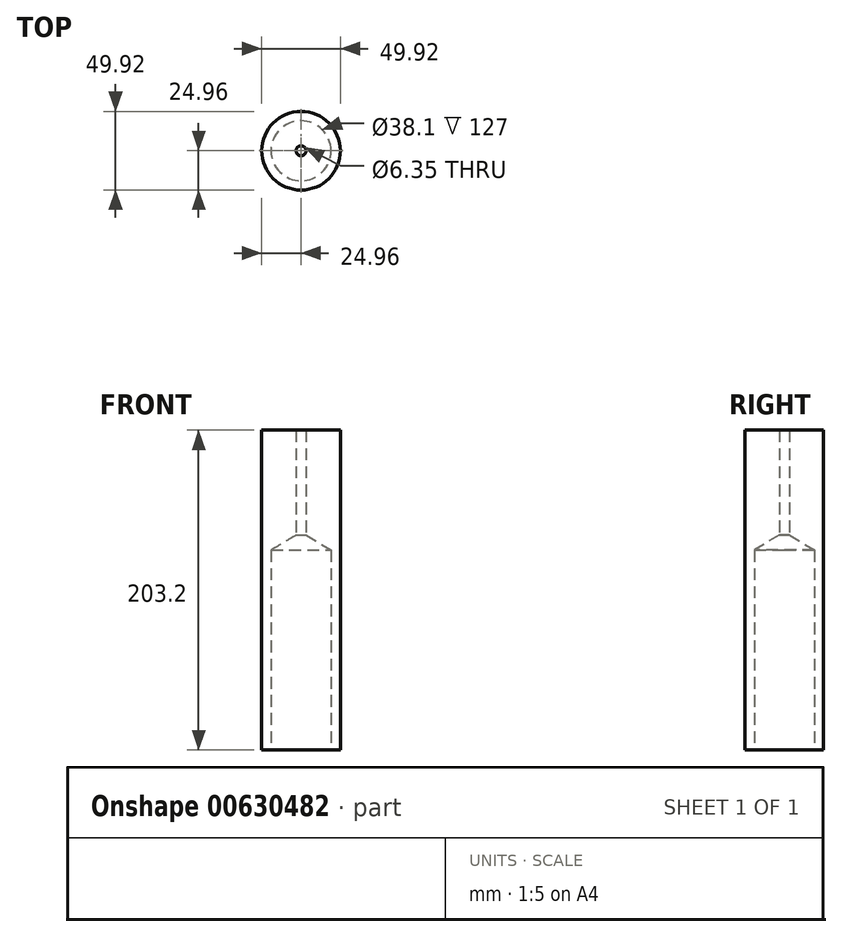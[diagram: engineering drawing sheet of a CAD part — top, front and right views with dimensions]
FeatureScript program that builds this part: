
annotation { "Feature Type Name" : "Feature", "Feature Type Description" : "" }
export const myFeature = defineFeature(function(context is Context, id is Id, definition is map)
    precondition{}
    {
        {
            var Q0;
            Q0=qCreatedBy(makeId("Top.planeOp"),FACE);
            var sketch = newSketch(context, id + "F0", { "sketchPlane" : qUnion([Q0])});
            skLineSegment(sketch, "E0.bottom", {"start": v(24.95, 25.85) * mm, "end": v(-24.95, 25.85) * mm});
            skLineSegment(sketch, "E0.top", {"start": v(24.95, -25.85) * mm, "end": v(-24.95, -25.85) * mm});
            skLineSegment(sketch, "E0.left", {"start": v(24.95, 25.85) * mm, "end": v(24.95, -25.85) * mm});
            skLineSegment(sketch, "E0.right", {"start": v(-24.95, 25.85) * mm, "end": v(-24.95, -25.85) * mm});
            skPoint(sketch, "E0.middle", {"position": v(0, 0) * mm});
            skSolve(sketch);
        }
        {
            var Q0;
            Q0=qCreatedBy(makeId("Top.planeOp"),FACE);
            var sketch = newSketch(context, id + "F1", { "sketchPlane" : qUnion([Q0])});
            skCircle(sketch, "E1", {"center": v(0, 0) * mm, "radius": 24.96 * mm});
            skSolve(sketch);
        }
        {
            var Q0;
            Q0 = qSketchRegion(id + "F1", true);
            extrude(context, id + "F2", {"entities" : qUnion([Q0]), "depth" : 203.2 * mm, "offsetDistance" : 25.4 * mm});
        }
        {
            var Q0;
            Q0=sQuery(id+"F0.wireOp",VERTEX,"E0.middle");
            var Q1;
            Q1=makeQuery(id+"F2.opExtrude","SWEPT_BODY",BODY,{"disambiguationData":[OSD([sQuery(id+"F1.wireOp",EDGE,"E1")])]});
            hole(context, id + "F3", {"style" : HoleStyle.SIMPLE, "endStyle" : HoleEndStyle.BLIND, "oppositeDirection" : true, "holeDiameter" : 38.1 * mm, "majorDiameter" : 6.35 * mm, "holeDepth" : 127 * mm, "isTappedThrough" : true, "tappedDepth" : 12.7 * mm, "tapClearance" : 3, "locations" : qUnion([Q0]), "scope" : qUnion([Q1])});
        }
        {
            var Q0;
            Q0=qCreatedBy(makeId("Top.planeOp"),FACE);
            var sketch = newSketch(context, id + "F4", { "sketchPlane" : qUnion([Q0])});
            skPoint(sketch, "E2", {"position": v(0, 0) * mm});
            skSolve(sketch);
        }
        {
            var Q0;
            Q0=sQuery(id+"F4.wireOp",VERTEX,"E2");
            var Q1;
            Q1=makeQuery(id+"F2.opExtrude","SWEPT_BODY",BODY,{"disambiguationData":[OSD([sQuery(id+"F1.wireOp",EDGE,"E1")])]});
            hole(context, id + "F5", {"style" : HoleStyle.SIMPLE, "endStyle" : HoleEndStyle.THROUGH, "oppositeDirection" : true, "holeDiameter" : 6.35 * mm, "majorDiameter" : 6.35 * mm, "isTappedThrough" : true, "tappedDepth" : 12.7 * mm, "tapClearance" : 3, "locations" : qUnion([Q0]), "scope" : qUnion([Q1])});
        }
    });
